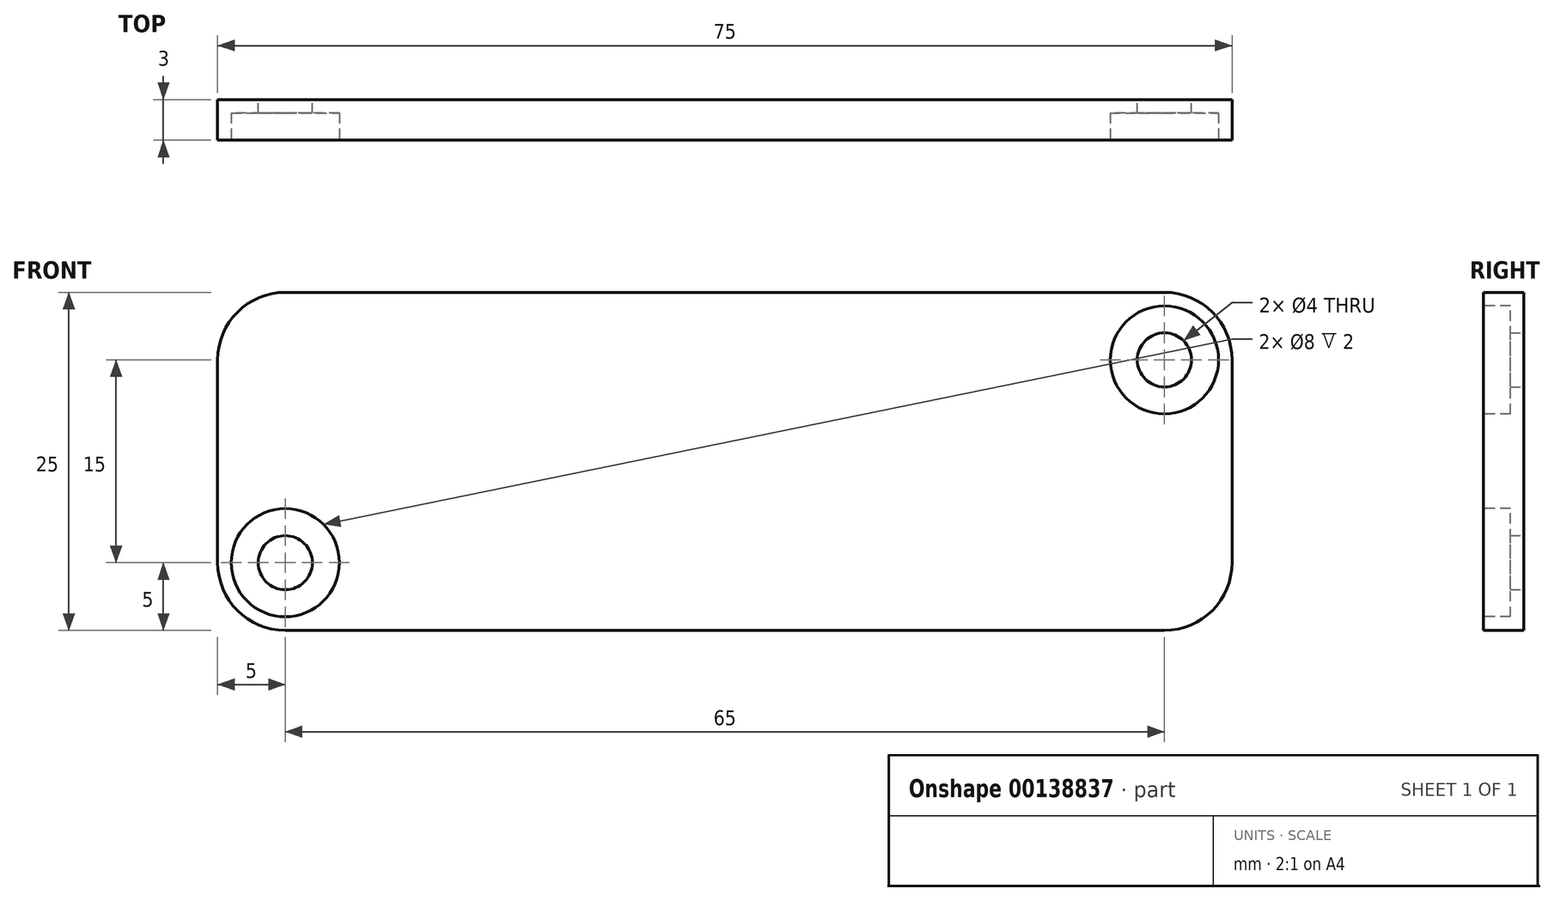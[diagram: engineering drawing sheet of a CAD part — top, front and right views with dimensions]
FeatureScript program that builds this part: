
annotation { "Feature Type Name" : "Feature", "Feature Type Description" : "" }
export const myFeature = defineFeature(function(context is Context, id is Id, definition is map)
    precondition{}
    {
        {
            var Q0;
            Q0=qCreatedBy(makeId("Front.planeOp"),FACE);
            var sketch = newSketch(context, id + "F0", { "sketchPlane" : qUnion([Q0])});
            skLineSegment(sketch, "E0.bottom", {"start": v(5, 0) * mm, "end": v(70, 0) * mm});
            skLineSegment(sketch, "E0.top", {"start": v(5, 25) * mm, "end": v(70, 25) * mm});
            skLineSegment(sketch, "E0.left", {"start": v(0, 5) * mm, "end": v(0, 20) * mm});
            skLineSegment(sketch, "E0.right", {"start": v(75, 5) * mm, "end": v(75, 20) * mm});
            skPoint(sketch, "E1.visualSharp", {"position": v(0, 25) * mm});
            skArc(sketch, "E1.filletArc", {"start": v(5, 25) * mm, "mid": v(1.46, 23.54) * mm, "end": v(0, 20) * mm});
            skPoint(sketch, "E2.visualSharp", {"position": v(75, 25) * mm});
            skArc(sketch, "E2.filletArc", {"start": v(75, 20) * mm, "mid": v(73.54, 23.54) * mm, "end": v(70, 25) * mm});
            skPoint(sketch, "E3.visualSharp", {"position": v(75, 0) * mm});
            skArc(sketch, "E3.filletArc", {"start": v(70, 0) * mm, "mid": v(73.54, 1.46) * mm, "end": v(75, 5) * mm});
            skPoint(sketch, "E4.visualSharp", {"position": v(0, 0) * mm});
            skArc(sketch, "E4.filletArc", {"start": v(0, 5) * mm, "mid": v(1.46, 1.46) * mm, "end": v(5, 0) * mm});
            skCircle(sketch, "E5", {"center": v(5, 5) * mm, "radius": 2 * mm});
            skCircle(sketch, "E6", {"center": v(70, 20) * mm, "radius": 2 * mm});
            skSolve(sketch);
        }
        {
            var Q0;
            Q0=makeQuery(id+"F0.imprint","IMPRINT",FACE,{"disambiguationData":[TD([[makeQuery(id+"F0.imprint","IMPRINT",EDGE,{"derivedFrom":sQuery(id+"F0.wireOp",EDGE,"E0.bottom")}),1.0]])]});
            extrude(context, id + "F1", {"entities" : qUnion([Q0]), "depth" : 3 * mm});
        }
        {
            var Q0;
            Q0=makeQuery(id+"F1.opExtrude","CAP_FACE",FACE,{"disambiguationData":[OSD([sQuery(id+"F0.wireOp",EDGE,"E0.bottom"),sQuery(id+"F0.wireOp",EDGE,"E0.top"),sQuery(id+"F0.wireOp",EDGE,"E0.left"),sQuery(id+"F0.wireOp",EDGE,"E0.right"),sQuery(id+"F0.wireOp",EDGE,"E1.filletArc"),sQuery(id+"F0.wireOp",EDGE,"E2.filletArc"),sQuery(id+"F0.wireOp",EDGE,"E3.filletArc"),sQuery(id+"F0.wireOp",EDGE,"E4.filletArc"),sQuery(id+"F0.wireOp",EDGE,"E5")])],"isStart":false});
            var sketch = newSketch(context, id + "F2", { "sketchPlane" : qUnion([Q0])});
            skCircle(sketch, "E7", {"center": v(5, 5) * mm, "radius": 4 * mm});
            skCircle(sketch, "E8", {"center": v(70, 20) * mm, "radius": 4 * mm});
            skSolve(sketch);
        }
        {
            var Q0;
            Q0 = qSketchRegion(id + "F2", true);
            extrude(context, id + "F3", {"entities" : qUnion([Q0]), "operationType" : NewBodyOperationType.REMOVE, "oppositeDirection" : true, "depth" : 2 * mm});
        }
    });
